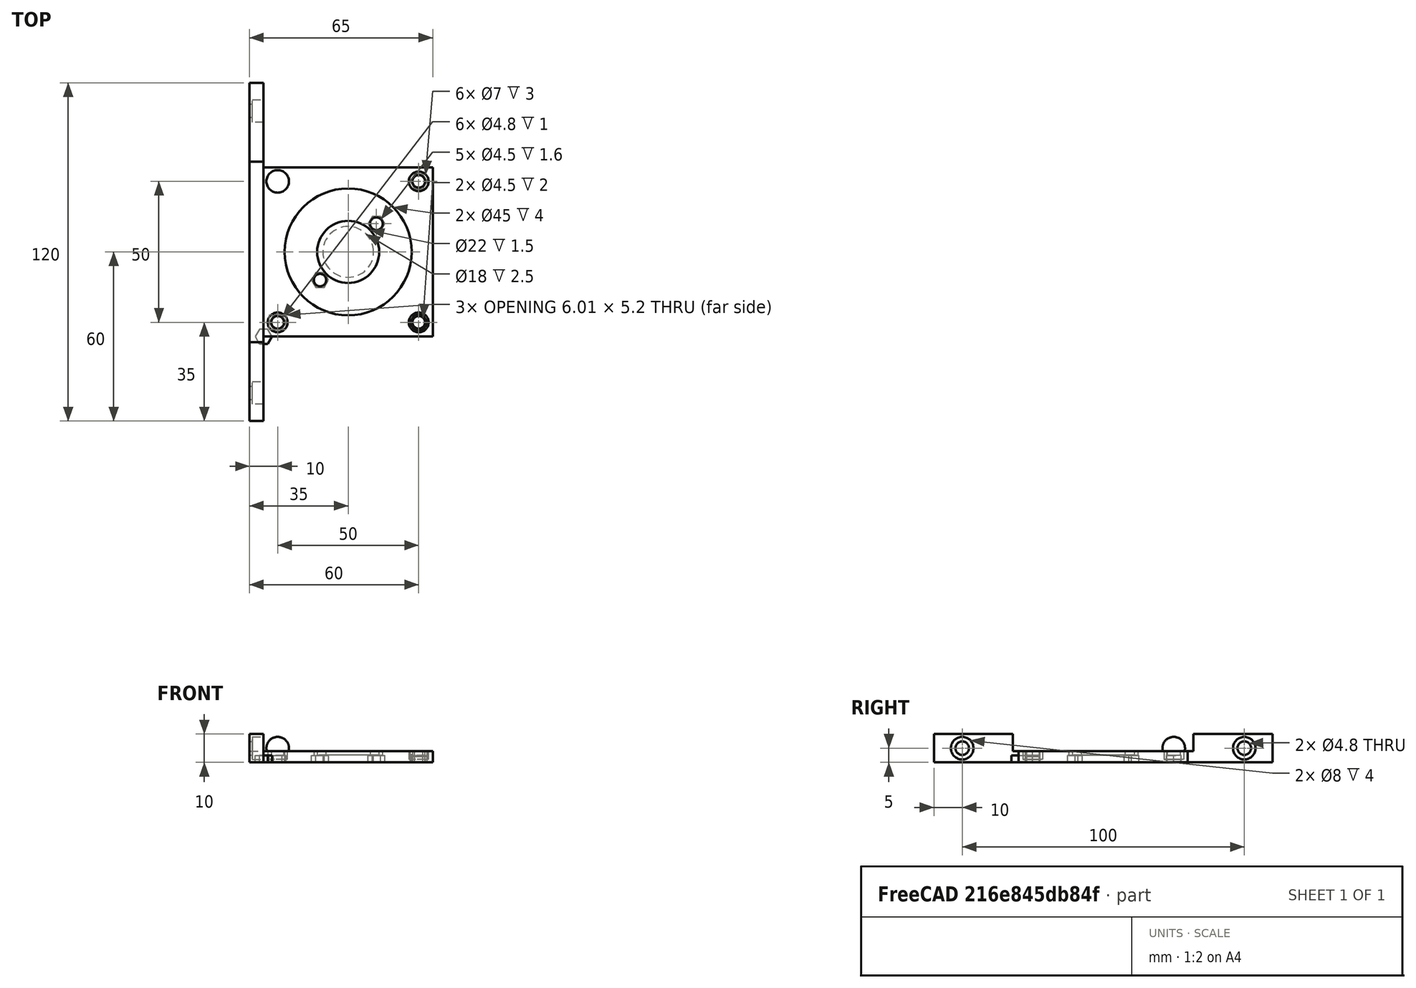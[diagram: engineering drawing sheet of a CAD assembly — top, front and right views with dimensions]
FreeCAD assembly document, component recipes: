
FREECAD ASSEMBLY — COMPONENT RECIPES ("KinematicMount01")

This assembly document has 6 components, labeled P0..P5 below (a component is one placed body or linked part). 0 of them carry a construction recipe — the FreeCAD feature program that regenerates the part from scratch, quoted from this document or its linked companion documents; the rest are supplied as boundary geometry only. No exploded tour is included for this assembly.
COMPONENT P0 — geometry summary ("DIN934_M4"; no construction recipe available for this part):
  bounding box: 6.0 x 5.2 x 2.4 mm
  tessellated surface: 20 triangles
  volume: 56 mm^3 (75% of its bounding box)
  symmetry: 2-fold rotationally symmetric about the x axis; 2-fold rotationally symmetric about the y axis; 6-fold rotationally symmetric about the z axis; mirror-symmetric across its x mid-plane, y mid-plane, z mid-plane
COMPONENT P1 — geometry summary ("DIN934_M005"; no construction recipe available for this part):
  bounding box: 6.0 x 5.2 x 2.4 mm
  tessellated surface: 20 triangles
  volume: 56 mm^3 (75% of its bounding box)
  symmetry: 2-fold rotationally symmetric about the x axis; 2-fold rotationally symmetric about the y axis; 6-fold rotationally symmetric about the z axis; mirror-symmetric across its x mid-plane, y mid-plane, z mid-plane
COMPONENT P2 — geometry summary ("DIN934_M006"; no construction recipe available for this part):
  bounding box: 6.0 x 5.2 x 2.4 mm
  tessellated surface: 20 triangles
  volume: 56 mm^3 (75% of its bounding box)
  symmetry: 2-fold rotationally symmetric about the x axis; 2-fold rotationally symmetric about the y axis; 6-fold rotationally symmetric about the z axis; mirror-symmetric across its x mid-plane, y mid-plane, z mid-plane
COMPONENT P3 — geometry summary ("DIN934_M008"; no construction recipe available for this part):
  bounding box: 6.0 x 5.2 x 2.4 mm
  tessellated surface: 20 triangles
  volume: 56 mm^3 (75% of its bounding box)
  symmetry: 2-fold rotationally symmetric about the x axis; 2-fold rotationally symmetric about the y axis; 6-fold rotationally symmetric about the z axis; mirror-symmetric across its x mid-plane, y mid-plane, z mid-plane
COMPONENT P4 — geometry summary ("DIN934_M009"; no construction recipe available for this part):
  bounding box: 6.0 x 5.2 x 2.4 mm
  tessellated surface: 20 triangles
  volume: 56 mm^3 (75% of its bounding box)
  symmetry: 2-fold rotationally symmetric about the x axis; 2-fold rotationally symmetric about the y axis; 6-fold rotationally symmetric about the z axis; mirror-symmetric across its x mid-plane, y mid-plane, z mid-plane
COMPONENT P5 — geometry summary ("DIN934_M010"; no construction recipe available for this part):
  bounding box: 6.0 x 5.2 x 2.4 mm
  tessellated surface: 20 triangles
  volume: 56 mm^3 (75% of its bounding box)
  symmetry: 2-fold rotationally symmetric about the x axis; 2-fold rotationally symmetric about the y axis; 6-fold rotationally symmetric about the z axis; mirror-symmetric across its x mid-plane, y mid-plane, z mid-plane
PROVENANCE & LICENSES
A FreeCAD (.FCStd) document from a public repository crawl; recipes are the document's own serialized feature recipes (and, for linked parts, companion documents' recipes).
License: bsd.
